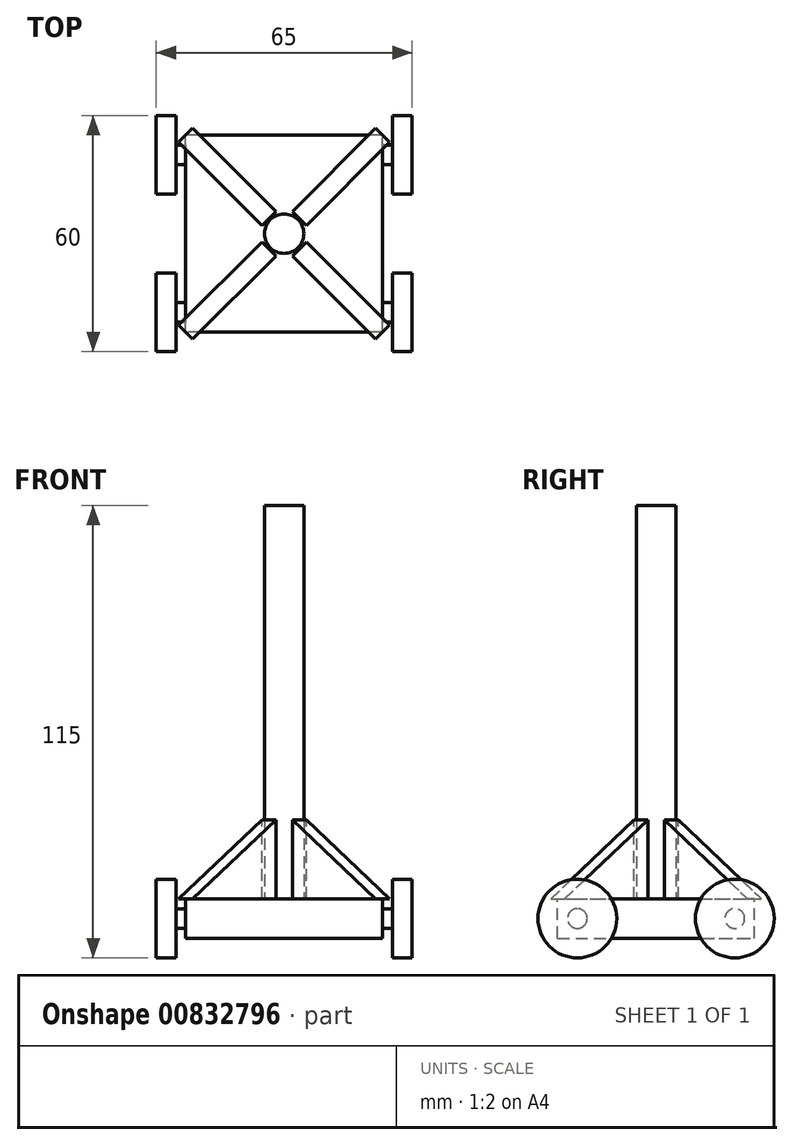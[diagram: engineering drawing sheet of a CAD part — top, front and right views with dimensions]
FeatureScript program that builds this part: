
annotation { "Feature Type Name" : "Feature", "Feature Type Description" : "" }
export const myFeature = defineFeature(function(context is Context, id is Id, definition is map)
    precondition{}
    {
        {
            var Q0;
            Q0=qCreatedBy(makeId("Top.planeOp"),FACE);
            var sketch = newSketch(context, id + "F0", { "sketchPlane" : qUnion([Q0])});
            skCircle(sketch, "E0", {"center": v(0, 0) * mm, "radius": 5 * mm});
            skSolve(sketch);
        }
        {
            var Q0;
            Q0 = qSketchRegion(id + "F0", true);
            extrude(context, id + "F1", {"entities" : qUnion([Q0]), "depth" : 100 * mm, "offsetDistance" : 25 * mm});
        }
        {
            var Q0;
            Q0=qCreatedBy(makeId("Top.planeOp"),FACE);
            var sketch = newSketch(context, id + "F2", { "sketchPlane" : qUnion([Q0])});
            skLineSegment(sketch, "E1.bottom", {"start": v(25, -25) * mm, "end": v(-25, -25) * mm});
            skLineSegment(sketch, "E1.top", {"start": v(25, 25) * mm, "end": v(-25, 25) * mm});
            skLineSegment(sketch, "E1.left", {"start": v(25, -25) * mm, "end": v(25, 25) * mm});
            skLineSegment(sketch, "E1.right", {"start": v(-25, -25) * mm, "end": v(-25, 25) * mm});
            skPoint(sketch, "E1.middle", {"position": v(0, 0) * mm});
            skSolve(sketch);
        }
        {
            var Q0;
            Q0 = qSketchRegion(id + "F2", true);
            extrude(context, id + "F3", {"entities" : qUnion([Q0]), "operationType" : NewBodyOperationType.ADD, "oppositeDirection" : true, "depth" : 10 * mm, "offsetDistance" : 25 * mm});
        }
        {
            var Q0;
            Q0=makeQuery(id+"F3.opExtrude","SWEPT_FACE",FACE,{"disambiguationData":[OSD([sQuery(id+"F2.wireOp",EDGE,"E1.left")])]});
            var sketch = newSketch(context, id + "F4", { "sketchPlane" : qUnion([Q0])});
            skLineSegment(sketch, "E2", {"start": v(-25, 0) * mm, "end": v(-15, -10) * mm, "construction": true});
            skLineSegment(sketch, "E3", {"start": v(-25, -10) * mm, "end": v(-15, 0) * mm, "construction": true});
            skLineSegment(sketch, "E4", {"start": v(-20, -5) * mm, "end": v(37.46, -5) * mm, "construction": true});
            skLineSegment(sketch, "E5", {"start": v(25, 0) * mm, "end": v(15, -10) * mm, "construction": true});
            skLineSegment(sketch, "E6", {"start": v(25, -10) * mm, "end": v(15, 0) * mm, "construction": true});
            skCircle(sketch, "E7", {"center": v(-20, -5) * mm, "radius": 2.5 * mm});
            skCircle(sketch, "E8", {"center": v(20, -5) * mm, "radius": 2.5 * mm});
            skSolve(sketch);
        }
        {
            var Q0;
            Q0 = qSketchRegion(id + "F4", true);
            extrude(context, id + "F5", {"entities" : qUnion([Q0]), "operationType" : NewBodyOperationType.ADD, "depth" : 2.5 * mm, "offsetDistance" : 25 * mm});
        }
        {
            var Q0;
            Q0=makeQuery(id+"F5.opExtrude","CAP_FACE",FACE,{"disambiguationData":[OSD([sQuery(id+"F4.wireOp",EDGE,"E7")])],"isStart":false});
            var sketch = newSketch(context, id + "F6", { "sketchPlane" : qUnion([Q0])});
            skCircle(sketch, "E9", {"center": v(-20, -5) * mm, "radius": 10 * mm});
            skSolve(sketch);
        }
        {
            var Q0;
            Q0 = qSketchRegion(id + "F6", true);
            extrude(context, id + "F7", {"entities" : qUnion([Q0]), "operationType" : NewBodyOperationType.ADD, "depth" : 5 * mm, "offsetDistance" : 25 * mm});
        }
        {
            var Q0;
            Q0=makeQuery(id+"F5.opExtrude","CAP_FACE",FACE,{"disambiguationData":[OSD([sQuery(id+"F4.wireOp",EDGE,"E8")])],"isStart":false});
            var sketch = newSketch(context, id + "F8", { "sketchPlane" : qUnion([Q0])});
            skCircle(sketch, "E10", {"center": v(20, -5) * mm, "radius": 10 * mm});
            skSolve(sketch);
        }
        {
            var Q0;
            Q0 = qSketchRegion(id + "F8", true);
            extrude(context, id + "F9", {"entities" : qUnion([Q0]), "operationType" : NewBodyOperationType.ADD, "depth" : 5 * mm, "offsetDistance" : 25 * mm});
        }
        {
            var Q0;
            Q0=makeQuery(id+"F3.opExtrude","SWEPT_FACE",FACE,{"disambiguationData":[OSD([sQuery(id+"F2.wireOp",EDGE,"E1.right")])]});
            var sketch = newSketch(context, id + "F10", { "sketchPlane" : qUnion([Q0])});
            skLineSegment(sketch, "E11", {"start": v(-25, -5) * mm, "end": v(25, -5) * mm, "construction": true});
            skLineSegment(sketch, "E12", {"start": v(-25, 0) * mm, "end": v(-15, -10) * mm, "construction": true});
            skLineSegment(sketch, "E13", {"start": v(-25, -10) * mm, "end": v(-15, 0) * mm, "construction": true});
            skLineSegment(sketch, "E14", {"start": v(25, -10) * mm, "end": v(15, 0) * mm, "construction": true});
            skLineSegment(sketch, "E15", {"start": v(25, 0) * mm, "end": v(15, -10) * mm, "construction": true});
            skCircle(sketch, "E16", {"center": v(-20, -5) * mm, "radius": 2.5 * mm});
            skCircle(sketch, "E17", {"center": v(20, -5) * mm, "radius": 2.5 * mm});
            skSolve(sketch);
        }
        {
            var Q0;
            Q0 = qSketchRegion(id + "F10", true);
            extrude(context, id + "F11", {"entities" : qUnion([Q0]), "operationType" : NewBodyOperationType.ADD, "depth" : 2.5 * mm, "offsetDistance" : 25 * mm});
        }
        {
            var Q0;
            Q0=makeQuery(id+"F11.opExtrude","CAP_FACE",FACE,{"disambiguationData":[OSD([sQuery(id+"F10.wireOp",EDGE,"E16")])],"isStart":false});
            var sketch = newSketch(context, id + "F12", { "sketchPlane" : qUnion([Q0])});
            skCircle(sketch, "E18", {"center": v(-20, -5) * mm, "radius": 10 * mm});
            skSolve(sketch);
        }
        {
            var Q0;
            Q0 = qSketchRegion(id + "F12", true);
            extrude(context, id + "F13", {"entities" : qUnion([Q0]), "operationType" : NewBodyOperationType.ADD, "depth" : 5 * mm, "offsetDistance" : 25 * mm});
        }
        {
            var Q0;
            Q0=makeQuery(id+"F11.opExtrude","CAP_FACE",FACE,{"disambiguationData":[OSD([sQuery(id+"F10.wireOp",EDGE,"E17")])],"isStart":false});
            var sketch = newSketch(context, id + "F14", { "sketchPlane" : qUnion([Q0])});
            skCircle(sketch, "E19", {"center": v(20, -5) * mm, "radius": 10 * mm});
            skSolve(sketch);
        }
        {
            var Q0;
            Q0 = qSketchRegion(id + "F14", true);
            extrude(context, id + "F15", {"entities" : qUnion([Q0]), "operationType" : NewBodyOperationType.ADD, "depth" : 5 * mm, "offsetDistance" : 25 * mm});
        }
        {
            var Q0;
            Q0=makeQuery(id+"F3.opExtrude","CAP_FACE",FACE,{"disambiguationData":[OSD([sQuery(id+"F2.wireOp",EDGE,"E1.bottom"),sQuery(id+"F2.wireOp",EDGE,"E1.top"),sQuery(id+"F2.wireOp",EDGE,"E1.left"),sQuery(id+"F2.wireOp",EDGE,"E1.right")])],"isStart":true});
            var sketch = newSketch(context, id + "F16", { "sketchPlane" : qUnion([Q0])});
            skLineSegment(sketch, "E20", {"start": v(0, 0) * mm, "end": v(-25, -25) * mm, "construction": true});
            skSolve(sketch);
        }
        {
            var Q0;
            Q0=makeQuery(id+"F1.opExtrude","CAP_FACE",FACE,{"disambiguationData":[OSD([sQuery(id+"F0.wireOp",EDGE,"E0")])],"isStart":false});
            var sketch = newSketch(context, id + "F17", { "sketchPlane" : qUnion([Q0])});
            skPoint(sketch, "E21", {"position": v(0, 0) * mm});
            skSolve(sketch);
        }
        {
            var Q0;
            Q0=sQuery(id+"F17.wireOp",VERTEX,"E21");
            var Q1;
            Q1=sQuery(id+"F16.wireOp",VERTEX,"E20.start");
            var Q2;
            Q2=sQuery(id+"F16.wireOp",VERTEX,"E20.end");
            cPlane(context, id + "F18", {"entities" : qUnion([Q0, Q1, Q2]), "cplaneType" : CPlaneType.THREE_POINT, "offset" : 25 * mm, "width" : 150 * mm, "height" : 150 * mm});
        }
        {
            var Q0;
            Q0=qCreatedBy(id+"F18.planeOp",FACE);
            var sketch = newSketch(context, id + "F19", { "sketchPlane" : qUnion([Q0])});
            skLineSegment(sketch, "E22", {"start": v(-35.36, 0) * mm, "end": v(-5.5, 0) * mm});
            skLineSegment(sketch, "E23", {"start": v(-5.5, 0) * mm, "end": v(-5.5, 20) * mm});
            skLineSegment(sketch, "E24", {"start": v(-35.36, 0) * mm, "end": v(-5.5, 20) * mm});
            skSolve(sketch);
        }
        {
            var Q0;
            Q0=makeQuery(id+"F19.imprint","IMPRINT",FACE,{"disambiguationData":[TD([[makeQuery(id+"F19.imprint","IMPRINT",EDGE,{"derivedFrom":sQuery(id+"F19.wireOp",EDGE,"E22")}),1.0]])]});
            extrude(context, id + "F20", {"entities" : qUnion([Q0]), "operationType" : NewBodyOperationType.ADD, "endBound" : BoundingType.SYMMETRIC, "depth" : 5 * mm, "offsetDistance" : 25 * mm});
        }
        {
            var Q0;
            Q0=makeQuery(id+"F16.imprint","IMPRINT",FACE,{"disambiguationData":[TD([[makeQuery(id+"F16.imprint","IMPRINT",EDGE,{"derivedFrom":makeQuery(id+"F3.opExtrude","CAP_EDGE",EDGE,{"disambiguationData":[OSD([sQuery(id+"F2.wireOp",EDGE,"E1.bottom")])],"isStart":true})}),-1.0]])]});
            var sketch = newSketch(context, id + "F21", { "sketchPlane" : qUnion([Q0])});
            skLineSegment(sketch, "E25", {"start": v(0, 0) * mm, "end": v(25, -25) * mm, "construction": true});
            skLineSegment(sketch, "E26", {"start": v(0, 0) * mm, "end": v(25, 25) * mm, "construction": true});
            skLineSegment(sketch, "E27", {"start": v(0, 0) * mm, "end": v(-25, 25) * mm, "construction": true});
            skSolve(sketch);
        }
        {
            var Q0;
            Q0=sQuery(id+"F16.wireOp",VERTEX,"E20.start");
            var Q1;
            Q1=sQuery(id+"F21.wireOp",VERTEX,"E25.end");
            var Q2;
            Q2=sQuery(id+"F17.wireOp",VERTEX,"E21");
            cPlane(context, id + "F22", {"entities" : qUnion([Q0, Q1, Q2]), "cplaneType" : CPlaneType.THREE_POINT, "offset" : 25 * mm, "width" : 150 * mm, "height" : 150 * mm});
        }
        {
            var Q0;
            Q0=qCreatedBy(id+"F22.planeOp",FACE);
            var sketch = newSketch(context, id + "F23", { "sketchPlane" : qUnion([Q0])});
            skLineSegment(sketch, "E28", {"start": v(-35.36, 0) * mm, "end": v(-35.36, 0) * mm});
            skLineSegment(sketch, "E29", {"start": v(5.5, 0) * mm, "end": v(35.36, 0) * mm});
            skLineSegment(sketch, "E30", {"start": v(5.5, 0) * mm, "end": v(5.5, 20) * mm});
            skLineSegment(sketch, "E31", {"start": v(5.5, 20) * mm, "end": v(35.36, 0) * mm});
            skLineSegment(sketch, "E32", {"start": v(-5.5, 0) * mm, "end": v(-35.36, 0) * mm});
            skLineSegment(sketch, "E33", {"start": v(-5.5, 0) * mm, "end": v(-5.5, 20) * mm});
            skLineSegment(sketch, "E34", {"start": v(-5.5, 20) * mm, "end": v(-35.36, 0) * mm});
            skSolve(sketch);
        }
        {
            var Q0;
            Q0 = qSketchRegion(id + "F23", true);
            extrude(context, id + "F24", {"entities" : qUnion([Q0]), "operationType" : NewBodyOperationType.ADD, "endBound" : BoundingType.SYMMETRIC, "depth" : 5 * mm, "offsetDistance" : 25 * mm});
        }
        {
            var Q0;
            Q0=qCreatedBy(id+"F18.planeOp",FACE);
            var sketch = newSketch(context, id + "F25", { "sketchPlane" : qUnion([Q0])});
            skLineSegment(sketch, "E35", {"start": v(5.5, 0) * mm, "end": v(35.36, 0) * mm});
            skLineSegment(sketch, "E36", {"start": v(5.5, 0) * mm, "end": v(5.5, 20) * mm});
            skLineSegment(sketch, "E37", {"start": v(5.5, 20) * mm, "end": v(35.36, 0) * mm});
            skSolve(sketch);
        }
        {
            var Q0;
            Q0 = qSketchRegion(id + "F25", true);
            extrude(context, id + "F26", {"entities" : qUnion([Q0]), "operationType" : NewBodyOperationType.ADD, "endBound" : BoundingType.SYMMETRIC, "depth" : 5 * mm, "offsetDistance" : 25 * mm});
        }
    });
